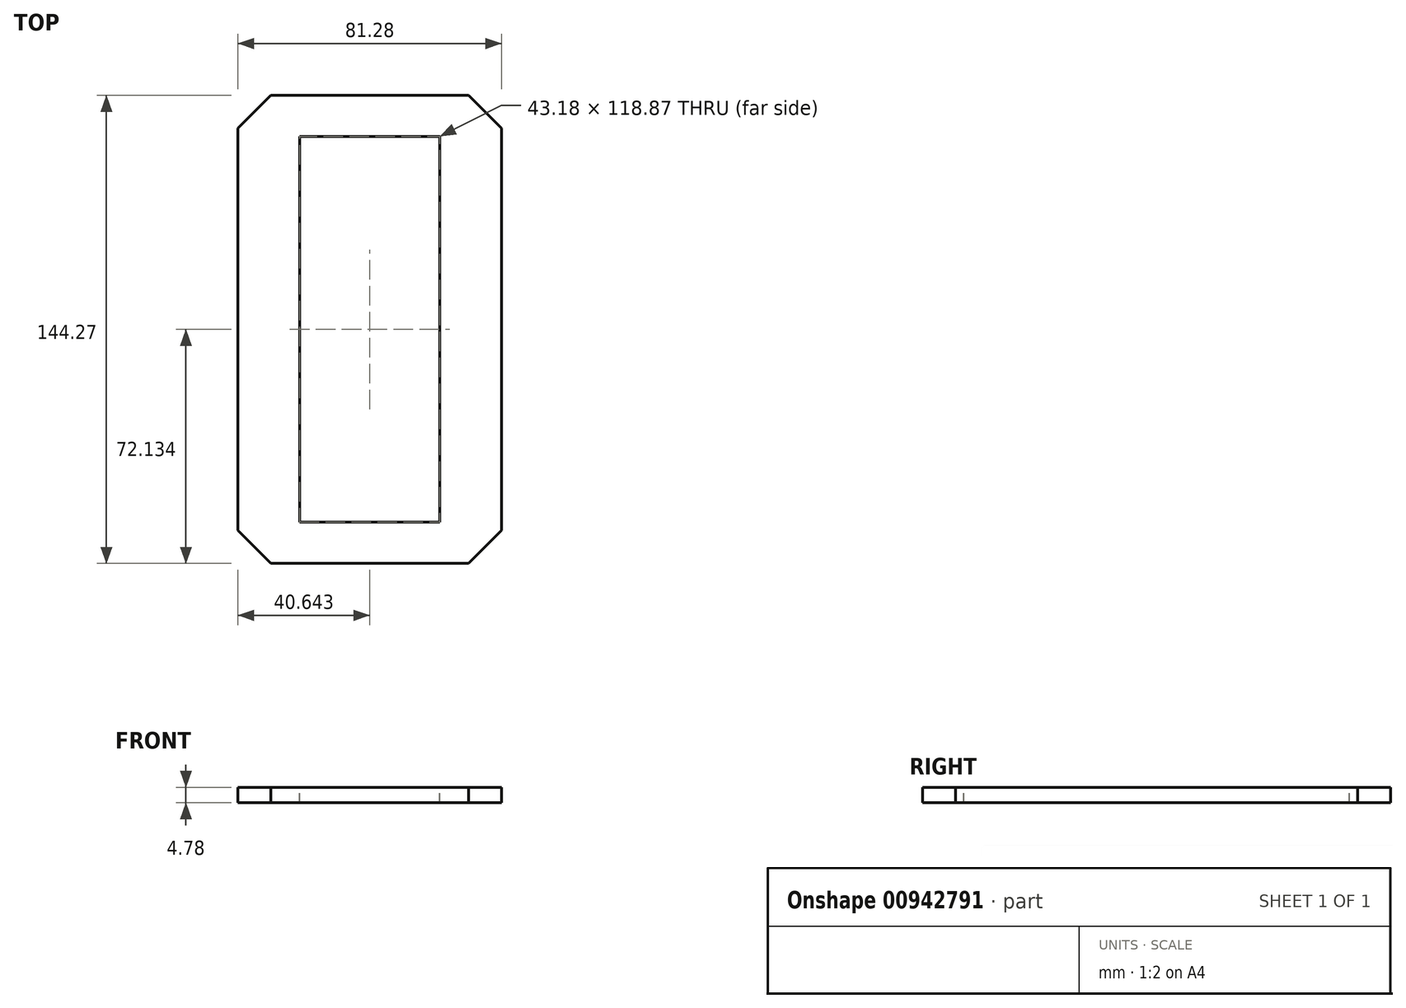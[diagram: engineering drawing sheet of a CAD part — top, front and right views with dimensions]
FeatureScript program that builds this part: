
annotation { "Feature Type Name" : "Feature", "Feature Type Description" : "" }
export const myFeature = defineFeature(function(context is Context, id is Id, definition is map)
    precondition{}
    {
        {
            var Q0;
            Q0=qCreatedBy(makeId("Top.planeOp"),FACE);
            var sketch = newSketch(context, id + "F0", { "sketchPlane" : qUnion([Q0])});
            skLineSegment(sketch, "E0.bottom", {"start": v(-43.2, 76.82) * mm, "end": v(38.08, 76.82) * mm});
            skLineSegment(sketch, "E0.top", {"start": v(-43.2, -67.45) * mm, "end": v(38.08, -67.45) * mm});
            skLineSegment(sketch, "E0.left", {"start": v(-43.2, 76.82) * mm, "end": v(-43.2, -67.45) * mm});
            skLineSegment(sketch, "E0.right", {"start": v(38.08, 76.82) * mm, "end": v(38.08, -67.45) * mm});
            skSolve(sketch);
        }
        {
            var Q0;
            Q0=makeQuery(id+"F0.imprint","IMPRINT",FACE,{"disambiguationData":[TD([[makeQuery(id+"F0.imprint","IMPRINT",EDGE,{"derivedFrom":sQuery(id+"F0.wireOp",EDGE,"E0.bottom")}),-1.0]])]});
            extrude(context, id + "F1", {"entities" : qUnion([Q0]), "depth" : 4.78 * mm, "offsetDistance" : 25.4 * mm});
        }
        {
            var Q0;
            Q0=makeQuery(id+"F1.opExtrude","CAP_FACE",FACE,{"disambiguationData":[OSD([sQuery(id+"F0.wireOp",EDGE,"E0.bottom"),sQuery(id+"F0.wireOp",EDGE,"E0.top"),sQuery(id+"F0.wireOp",EDGE,"E0.left"),sQuery(id+"F0.wireOp",EDGE,"E0.right")])],"isStart":false});
            var sketch = newSketch(context, id + "F2", { "sketchPlane" : qUnion([Q0])});
            skLineSegment(sketch, "E1.bottom", {"start": v(-24.15, 64.12) * mm, "end": v(19.03, 64.12) * mm});
            skLineSegment(sketch, "E1.top", {"start": v(-24.15, -54.75) * mm, "end": v(19.03, -54.75) * mm});
            skLineSegment(sketch, "E1.left", {"start": v(-24.15, 64.12) * mm, "end": v(-24.15, -54.75) * mm});
            skLineSegment(sketch, "E1.right", {"start": v(19.03, 64.12) * mm, "end": v(19.03, -54.75) * mm});
            skSolve(sketch);
        }
        {
            var Q0;
            Q0 = qSketchRegion(id + "F2", true);
            extrude(context, id + "F3", {"entities" : qUnion([Q0]), "operationType" : NewBodyOperationType.REMOVE, "oppositeDirection" : true, "depth" : 25.4 * mm, "offsetDistance" : 25.4 * mm});
        }
        {
            var Q0;
            Q0=makeQuery(id+"F1.opExtrude","SWEPT_EDGE",EDGE,{"disambiguationData":[OSD([sQuery(id+"F0.wireOp",EDGE,"E0.top"),sQuery(id+"F0.wireOp",EDGE,"E0.right")])]});
            var Q1;
            Q1=makeQuery(id+"F1.opExtrude","SWEPT_EDGE",EDGE,{"disambiguationData":[OSD([sQuery(id+"F0.wireOp",EDGE,"E0.top"),sQuery(id+"F0.wireOp",EDGE,"E0.left")])]});
            var Q2;
            Q2=makeQuery(id+"F1.opExtrude","SWEPT_EDGE",EDGE,{"disambiguationData":[OSD([sQuery(id+"F0.wireOp",EDGE,"E0.bottom"),sQuery(id+"F0.wireOp",EDGE,"E0.right")])]});
            var Q3;
            Q3=makeQuery(id+"F1.opExtrude","SWEPT_EDGE",EDGE,{"disambiguationData":[OSD([sQuery(id+"F0.wireOp",EDGE,"E0.bottom"),sQuery(id+"F0.wireOp",EDGE,"E0.left")])]});
            chamfer(context, id + "F4", {"entities" : qUnion([Q0, Q1, Q2, Q3]), "width" : 10.16 * mm, "tangentPropagation" : true});
        }
    });
